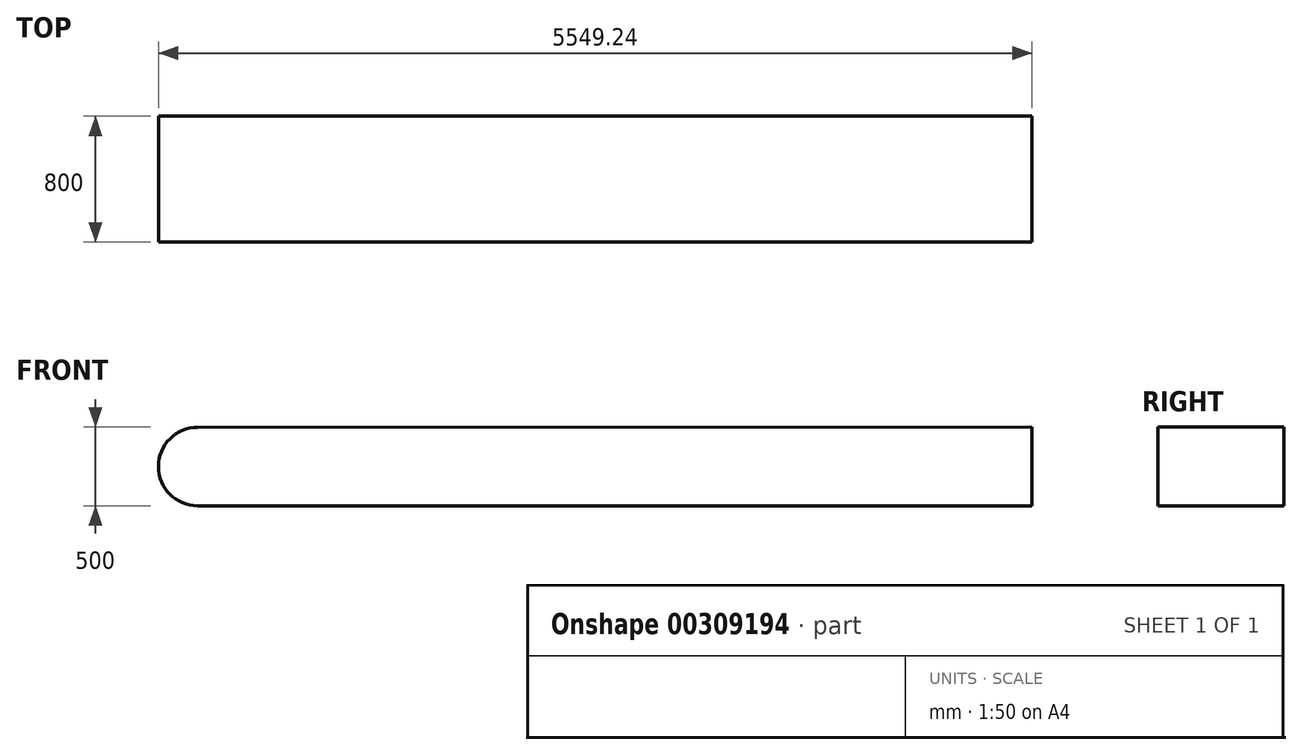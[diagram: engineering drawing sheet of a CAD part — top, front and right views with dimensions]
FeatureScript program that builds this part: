
annotation { "Feature Type Name" : "Feature", "Feature Type Description" : "" }
export const myFeature = defineFeature(function(context is Context, id is Id, definition is map)
    precondition{}
    {
        {
            var Q0;
            Q0=qCreatedBy(makeId("Front.planeOp"),FACE);
            var sketch = newSketch(context, id + "F0", { "sketchPlane" : qUnion([Q0])});
            skLineSegment(sketch, "E0", {"start": v(-1499.32, 287.89) * mm, "end": v(3800.68, 289.41) * mm});
            skLineSegment(sketch, "E1", {"start": v(3800.68, 289.41) * mm, "end": v(3800.68, -210.59) * mm});
            skLineSegment(sketch, "E2", {"start": v(3800.68, -210.59) * mm, "end": v(-1499.32, -210.59) * mm});
            skArc(sketch, "E3", {"start": v(-1499.32, 287.89) * mm, "mid": v(-1748.56, 38.65) * mm, "end": v(-1499.32, -210.59) * mm});
            skLineSegment(sketch, "E4", {"start": v(-1499.32, 287.89) * mm, "end": v(-1499.32, -210.59) * mm, "construction": true});
            skSolve(sketch);
        }
        {
            var Q0;
            Q0=qSketchRegion(id+"F0",true);
            extrude(context, id + "F1", {"entities" : qUnion([Q0]), "depth" : 800 * mm});
        }
    });
